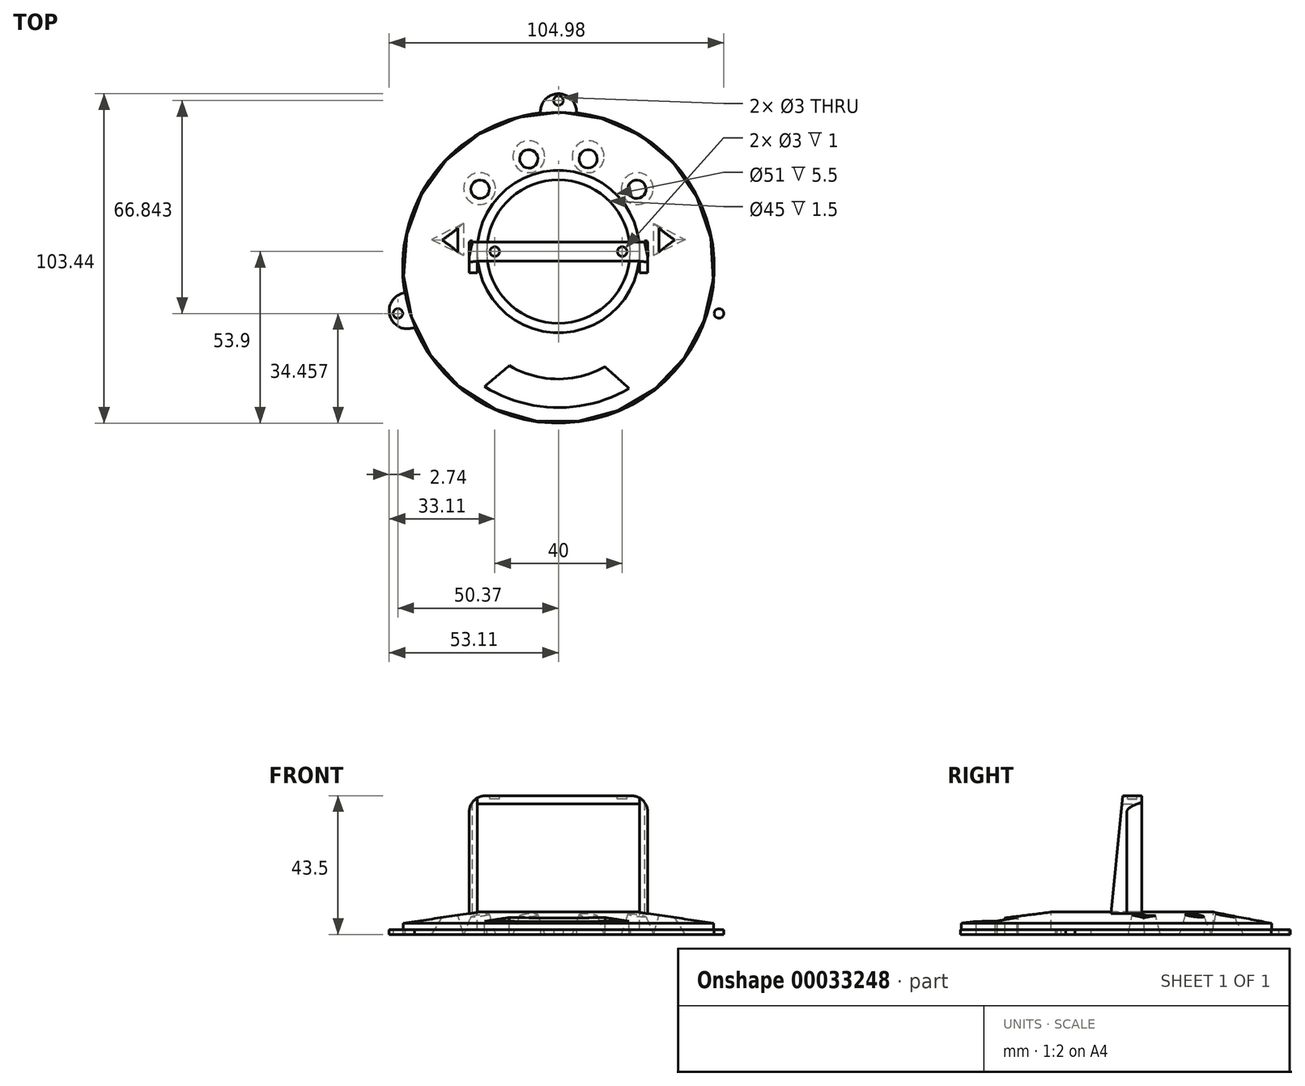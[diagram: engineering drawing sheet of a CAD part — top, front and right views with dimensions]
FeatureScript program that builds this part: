
annotation { "Feature Type Name" : "Feature", "Feature Type Description" : "" }
export const myFeature = defineFeature(function(context is Context, id is Id, definition is map)
    precondition{}
    {
        {
            var Q0;
            Q0=qCreatedBy(makeId("Top.planeOp"),FACE);
            var sketch = newSketch(context, id + "F0", { "sketchPlane" : qUnion([Q0])});
            skCircle(sketch, "E0", {"center": v(0, 0) * mm, "radius": 48.9 * mm});
            skArc(sketch, "E1", {"start": v(5.63, 48.57) * mm, "mid": v(0, 54.54) * mm, "end": v(-5.63, 48.57) * mm});
            skLineSegment(sketch, "E2", {"start": v(0, 48.9) * mm, "end": v(0, 52.4) * mm, "construction": true});
            skCircle(sketch, "E3", {"center": v(0, 52.4) * mm, "radius": 1.5 * mm});
            skCircle(sketch, "E4", {"center": v(-50.37, -14.44) * mm, "radius": 1.5 * mm});
            skArc(sketch, "E5", {"start": v(-48.24, -8.02) * mm, "mid": v(-52.9, -15.17) * mm, "end": v(-45.16, -18.76) * mm});
            skCircle(sketch, "E6.MirrorC", {"center": v(50.37, -14.44) * mm, "radius": 1.5 * mm});
            skArc(sketch, "E7.MirrorCS", {"start": v(48.24, -8.02) * mm, "mid": v(52.9, -15.17) * mm, "end": v(45.16, -18.76) * mm});
            skLineSegment(sketch, "E8", {"start": v(0, 0) * mm, "end": v(50.37, -14.44) * mm, "construction": true});
            skLineSegment(sketch, "E9", {"start": v(0, 0) * mm, "end": v(48.9, 0) * mm, "construction": true});
            skLineSegment(sketch, "E10.MirrorCS", {"start": v(0, 0) * mm, "end": v(-50.37, -14.44) * mm, "construction": true});
            skLineSegment(sketch, "E11.MirrorCS", {"start": v(0, 0) * mm, "end": v(-48.9, 0) * mm, "construction": true});
            skSolve(sketch);
        }
        {
            var Q0;
            {var subQ0=sQuery(id+"F0.wireOp",EDGE,"E0");var subQ12=makeQuery(id+"F0.imprint","IMPRINT",VERTEX,{"disambiguationData":[OD(0.0)],"derivedFrom":subQ0});Q0=makeQuery(id+"F0.imprint","IMPRINT",FACE,{"disambiguationData":[TD([[makeQuery(id+"F0.imprint","IMPRINT",EDGE,{"disambiguationData":[TD([[subQ12,1.0]])],"derivedFrom":subQ0}),1.0]])]});}
            var Q1;
            {var subQ0=sQuery(id+"F0.wireOp",EDGE,"E1");Q1=makeQuery(id+"F0.imprint","IMPRINT",FACE,{"disambiguationData":[TD([[makeQuery(id+"F0.imprint","IMPRINT",EDGE,{"derivedFrom":subQ0}),1.0]])]});}
            var Q2;
            {var subQ0=sQuery(id+"F0.wireOp",EDGE,"752fcca0-ccf0-49d4-acc3-ab4a65df21e3.2.0");Q2=makeQuery(id+"F0.imprint","IMPRINT",FACE,{"disambiguationData":[TD([[makeQuery(id+"F0.imprint","IMPRINT",EDGE,{"derivedFrom":subQ0}),1.0]])]});}
            var Q3;
            {var subQ0=sQuery(id+"F0.wireOp",EDGE,"752fcca0-ccf0-49d4-acc3-ab4a65df21e3.1.0");Q3=makeQuery(id+"F0.imprint","IMPRINT",FACE,{"disambiguationData":[TD([[makeQuery(id+"F0.imprint","IMPRINT",EDGE,{"derivedFrom":subQ0}),1.0]])]});}
            var Q4;
            Q4=makeQuery(id+"F0.imprint","IMPRINT",FACE,{"disambiguationData":[TD([[makeQuery(id+"F0.imprint","IMPRINT",EDGE,{"derivedFrom":sQuery(id+"F0.wireOp",EDGE,"E4")}),-1.0]])]});
            var Q5;
            Q5=makeQuery(id+"F0.imprint","IMPRINT",FACE,{"disambiguationData":[TD([[makeQuery(id+"F0.imprint","IMPRINT",EDGE,{"derivedFrom":sQuery(id+"F0.wireOp",EDGE,"E6.MirrorC")}),1.0]])]});
            var Q6;
            {var subQ0=sQuery(id+"F0.wireOp",EDGE,"E0");var subQ3=sQuery(id+"F0.wireOp",EDGE,"E1");var subQ4=makeQuery(id+"F0.imprint","INTERSECT",VERTEX,{"disambiguationData":[OD(0.0)],"derivedFrom":[subQ0,subQ3]});Q6=makeQuery(id+"F0.imprint","IMPRINT",FACE,{"disambiguationData":[TD([[makeQuery(id+"F0.imprint","IMPRINT",EDGE,{"disambiguationData":[TD([[subQ4,-1.0]])],"derivedFrom":subQ0}),1.0]])]});}
            extrude(context, id + "F1", {"entities" : qUnion([Q0, Q1, Q2, Q3, Q4, Q5, Q6]), "depth" : 1.5 * mm});
        }
        {
            var Q0;
            Q0=makeQuery(id+"F1.opExtrude","CAP_FACE",FACE,{"disambiguationData":[OSD([sQuery(id+"F0.wireOp",EDGE,"E0"),sQuery(id+"F0.wireOp",EDGE,"E1"),sQuery(id+"F0.wireOp",EDGE,"E3"),sQuery(id+"F0.wireOp",EDGE,"E4"),sQuery(id+"F0.wireOp",EDGE,"E5"),sQuery(id+"F0.wireOp",EDGE,"E6.MirrorC"),sQuery(id+"F0.wireOp",EDGE,"E7.MirrorCS")])],"isStart":false});
            var sketch = newSketch(context, id + "F2", { "sketchPlane" : qUnion([Q0])});
            skCircle(sketch, "E12", {"center": v(0, 0) * mm, "radius": 48.7 * mm});
            skSolve(sketch);
        }
        {
            var Q0;
            Q0=qSketchRegion(id+"F2",true);
            extrude(context, id + "F3", {"entities" : qUnion([Q0]), "operationType" : NewBodyOperationType.ADD, "depth" : 2 * mm});
        }
        {
            var Q0;
            Q0=qCreatedBy(makeId("Top.planeOp"),FACE);
            cPlane(context, id + "F4", {"entities" : qUnion([Q0]), "cplaneType" : CPlaneType.OFFSET, "offset" : 7 * mm, "width" : 150 * mm, "height" : 150 * mm});
        }
        {
            var Q0;
            Q0=qCreatedBy(id+"F4.planeOp",FACE);
            var sketch = newSketch(context, id + "F5", { "sketchPlane" : qUnion([Q0])});
            skCircle(sketch, "E13", {"center": v(0, 5) * mm, "radius": 25.5 * mm});
            skCircle(sketch, "E14.0", {"center": v(0, 52.4) * mm, "radius": 1.5 * mm});
            skLineSegment(sketch, "E15", {"start": v(0, 52.4) * mm, "end": v(0, 5) * mm, "construction": true});
            skSolve(sketch);
        }
        {
            var Q0;
            Q0=qCreatedBy(makeId("Top.planeOp"),FACE);
            var sketch = newSketch(context, id + "F6", { "sketchPlane" : qUnion([Q0])});
            skCircle(sketch, "E16", {"center": v(0, 0) * mm, "radius": 48.9 * mm});
            skSolve(sketch);
        }
        {
            var Q1;
            Q1=makeQuery(id+"F5.imprint","IMPRINT",FACE,{"disambiguationData":[TD([[makeQuery(id+"F5.imprint","IMPRINT",EDGE,{"derivedFrom":sQuery(id+"F5.wireOp",EDGE,"E13")}),1.0]])]});
            var Q2;
            Q2=makeQuery(id+"F3.opExtrude","CAP_FACE",FACE,{"disambiguationData":[OSD([sQuery(id+"F2.wireOp",EDGE,"E12")])],"isStart":false});
            loft(context, id + "F7", {"operationType" : NewBodyOperationType.ADD, "sheetProfilesArray" : [{ "sheetProfileEntities" : qUnion([Q1]) }, { "sheetProfileEntities" : qUnion([Q2]) }]});
        }
        {
            var Q0;
            Q0=makeQuery(id+"F1.opExtrude","CAP_FACE",FACE,{"disambiguationData":[OSD([sQuery(id+"F0.wireOp",EDGE,"E0"),sQuery(id+"F0.wireOp",EDGE,"E1"),sQuery(id+"F0.wireOp",EDGE,"E3"),sQuery(id+"F0.wireOp",EDGE,"752fcca0-ccf0-49d4-acc3-ab4a65df21e3.1.0"),sQuery(id+"F0.wireOp",EDGE,"752fcca0-ccf0-49d4-acc3-ab4a65df21e3.1.1"),sQuery(id+"F0.wireOp",EDGE,"752fcca0-ccf0-49d4-acc3-ab4a65df21e3.2.0"),sQuery(id+"F0.wireOp",EDGE,"752fcca0-ccf0-49d4-acc3-ab4a65df21e3.2.1")])],"isStart":false});
            var sketch = newSketch(context, id + "F8", { "sketchPlane" : qUnion([Q0])});
            skLineSegment(sketch, "E17", {"start": v(0, 0) * mm, "end": v(34, 0) * mm});
            skLineSegment(sketch, "E18", {"start": v(0, 0) * mm, "end": v(32.84, 8.8) * mm});
            skLineSegment(sketch, "E19", {"start": v(0, 0) * mm, "end": v(24.04, 24.04) * mm});
            skLineSegment(sketch, "E20", {"start": v(0, 0) * mm, "end": v(8.8, 32.84) * mm});
            skLineSegment(sketch, "E21", {"start": v(0, 0) * mm, "end": v(0, 34) * mm});
            skCircle(sketch, "E22", {"center": v(32.84, 8.8) * mm, "radius": 2.5 * mm});
            skCircle(sketch, "E23", {"center": v(24.04, 24.04) * mm, "radius": 2.5 * mm});
            skCircle(sketch, "E24", {"center": v(8.8, 32.84) * mm, "radius": 2.5 * mm});
            skCircle(sketch, "E25.MirrorC", {"center": v(-8.8, 32.84) * mm, "radius": 2.5 * mm});
            skCircle(sketch, "E26.MirrorC", {"center": v(-24.04, 24.04) * mm, "radius": 2.5 * mm});
            skCircle(sketch, "E27.MirrorC", {"center": v(-32.84, 8.8) * mm, "radius": 2.5 * mm});
            skSolve(sketch);
        }
        {
            var Q0;
            Q0=qCreatedBy(id+"F4.planeOp",FACE);
            var sketch = newSketch(context, id + "F9", { "sketchPlane" : qUnion([Q0])});
            skLineSegment(sketch, "E28", {"start": v(-24.4, 24.38) * mm, "end": v(0, 0) * mm, "construction": true});
            skLineSegment(sketch, "E29", {"start": v(0, 0) * mm, "end": v(-9.23, 33.76) * mm, "construction": true});
            skLineSegment(sketch, "E30", {"start": v(0, 0) * mm, "end": v(-31.88, 8.54) * mm, "construction": true});
            skLineSegment(sketch, "E31.MirrorCS", {"start": v(0, 0) * mm, "end": v(31.88, 8.54) * mm, "construction": true});
            skLineSegment(sketch, "E32.MirrorCS", {"start": v(24.4, 24.38) * mm, "end": v(0, 0) * mm, "construction": true});
            skLineSegment(sketch, "E33.MirrorCS", {"start": v(0, 0) * mm, "end": v(9.23, 33.76) * mm, "construction": true});
            skLineSegment(sketch, "E34", {"start": v(-31.88, 8.54) * mm, "end": v(-31.88, 12.04) * mm});
            skLineSegment(sketch, "E35", {"start": v(-31.88, 8.54) * mm, "end": v(-35.38, 8.54) * mm, "construction": true});
            skLineSegment(sketch, "E36", {"start": v(-31.88, 12.04) * mm, "end": v(-35.38, 8.54) * mm});
            skLineSegment(sketch, "E37.MirrorCS", {"start": v(-31.88, 5.04) * mm, "end": v(-35.38, 8.54) * mm});
            skLineSegment(sketch, "E38.MirrorCS", {"start": v(-31.88, 8.54) * mm, "end": v(-31.88, 5.04) * mm});
            skLineSegment(sketch, "E39.MirrorCS", {"start": v(31.88, 8.54) * mm, "end": v(31.88, 12.04) * mm});
            skLineSegment(sketch, "E40.MirrorCS", {"start": v(31.88, 12.04) * mm, "end": v(35.38, 8.54) * mm});
            skLineSegment(sketch, "E41.MirrorCS", {"start": v(31.88, 5.04) * mm, "end": v(35.38, 8.54) * mm});
            skLineSegment(sketch, "E42.MirrorCS", {"start": v(31.88, 8.54) * mm, "end": v(31.88, 5.04) * mm});
            skCircle(sketch, "E43", {"center": v(9.23, 33.76) * mm, "radius": 2.5 * mm});
            skCircle(sketch, "E44", {"center": v(-9.23, 33.76) * mm, "radius": 2.5 * mm});
            skCircle(sketch, "E45", {"center": v(-24.4, 24.38) * mm, "radius": 2.5 * mm});
            skCircle(sketch, "E46", {"center": v(24.4, 24.38) * mm, "radius": 2.5 * mm});
            skSolve(sketch);
        }
        {
            var Q0;
            Q0=makeQuery(id+"F1.opExtrude","CAP_FACE",FACE,{"disambiguationData":[OSD([sQuery(id+"F0.wireOp",EDGE,"E0"),sQuery(id+"F0.wireOp",EDGE,"E1"),sQuery(id+"F0.wireOp",EDGE,"E3"),sQuery(id+"F0.wireOp",EDGE,"752fcca0-ccf0-49d4-acc3-ab4a65df21e3.1.0"),sQuery(id+"F0.wireOp",EDGE,"752fcca0-ccf0-49d4-acc3-ab4a65df21e3.1.1"),sQuery(id+"F0.wireOp",EDGE,"752fcca0-ccf0-49d4-acc3-ab4a65df21e3.2.0"),sQuery(id+"F0.wireOp",EDGE,"752fcca0-ccf0-49d4-acc3-ab4a65df21e3.2.1")])],"isStart":false});
            var sketch = newSketch(context, id + "F10", { "sketchPlane" : qUnion([Q0])});
            skLineSegment(sketch, "E47", {"start": v(-15.4, -30.8) * mm, "end": v(-23.2, -37.4) * mm});
            skArc(sketch, "E48", {"start": v(-23.2, -37.4) * mm, "mid": v(-0.58, -44) * mm, "end": v(22.2, -37.99) * mm});
            skLineSegment(sketch, "E49", {"start": v(-15.4, -30.8) * mm, "end": v(14.6, -31.2) * mm, "construction": true});
            skLineSegment(sketch, "E50", {"start": v(0, 0) * mm, "end": v(-0.4, -31) * mm, "construction": true});
            skArc(sketch, "E51", {"start": v(-15.4, -30.8) * mm, "mid": v(-0.46, -35.02) * mm, "end": v(14.6, -31.2) * mm});
            skLineSegment(sketch, "E52.MirrorCS", {"start": v(14.6, -31.2) * mm, "end": v(22.2, -37.99) * mm});
            skSolve(sketch);
        }
        {
            var Q0;
            Q0=qSketchRegion(id+"F10",true);
            extrude(context, id + "F11", {"entities" : qUnion([Q0]), "operationType" : NewBodyOperationType.REMOVE, "endBound" : BoundingType.THROUGH_ALL, "oppositeDirection" : true, "depth" : 25 * mm, "hasSecondDirection" : true, "secondDirectionBound" : SecondDirectionBoundingType.THROUGH_ALL, "secondDirectionOppositeDirection" : false, "secondDirectionDepth" : 25 * mm});
        }
        {
            var Q0;
            Q0=makeQuery(id+"F1.opExtrude","CAP_FACE",FACE,{"disambiguationData":[OSD([sQuery(id+"F0.wireOp",EDGE,"E0"),sQuery(id+"F0.wireOp",EDGE,"E1"),sQuery(id+"F0.wireOp",EDGE,"E3"),sQuery(id+"F0.wireOp",EDGE,"752fcca0-ccf0-49d4-acc3-ab4a65df21e3.1.0"),sQuery(id+"F0.wireOp",EDGE,"752fcca0-ccf0-49d4-acc3-ab4a65df21e3.1.1"),sQuery(id+"F0.wireOp",EDGE,"752fcca0-ccf0-49d4-acc3-ab4a65df21e3.2.0"),sQuery(id+"F0.wireOp",EDGE,"752fcca0-ccf0-49d4-acc3-ab4a65df21e3.2.1")])],"isStart":true});
            var sketch = newSketch(context, id + "F12", { "sketchPlane" : qUnion([Q0])});
            skLineSegment(sketch, "E53.0", {"start": v(0, 0) * mm, "end": v(0, -34) * mm, "construction": true});
            skLineSegment(sketch, "E54", {"start": v(-32.84, -8.8) * mm, "end": v(-39.84, -8.8) * mm, "construction": true});
            skLineSegment(sketch, "E55", {"start": v(-29.84, -13.8) * mm, "end": v(-39.84, -8.8) * mm});
            skLineSegment(sketch, "E56", {"start": v(-32.84, -8.8) * mm, "end": v(-29.84, -8.8) * mm, "construction": true});
            skLineSegment(sketch, "E57", {"start": v(-29.84, -8.8) * mm, "end": v(-29.84, -13.8) * mm});
            skLineSegment(sketch, "E58", {"start": v(-29.84, -8.8) * mm, "end": v(-29.84, -3.8) * mm});
            skLineSegment(sketch, "E59", {"start": v(-39.84, -8.8) * mm, "end": v(-29.84, -3.8) * mm});
            skLineSegment(sketch, "E60.MirrorCS", {"start": v(29.84, -8.8) * mm, "end": v(29.84, -13.8) * mm});
            skLineSegment(sketch, "E61.MirrorCS", {"start": v(29.84, -13.8) * mm, "end": v(39.84, -8.8) * mm});
            skLineSegment(sketch, "E62.MirrorCS", {"start": v(39.84, -8.8) * mm, "end": v(29.84, -3.8) * mm});
            skLineSegment(sketch, "E63.MirrorCS", {"start": v(29.84, -8.8) * mm, "end": v(29.84, -3.8) * mm});
            skPoint(sketch, "E64.MirrorP", {"position": v(9.32, -34.77) * mm});
            skPoint(sketch, "E65.MirrorP", {"position": v(32.84, -8.8) * mm});
            skPoint(sketch, "E66.MirrorP", {"position": v(24.75, -24.75) * mm});
            skLineSegment(sketch, "E67", {"start": v(0, 0) * mm, "end": v(32.84, -8.8) * mm, "construction": true});
            skLineSegment(sketch, "E68", {"start": v(32.84, -8.8) * mm, "end": v(29.84, -8.8) * mm, "construction": true});
            skLineSegment(sketch, "E69", {"start": v(0, 0) * mm, "end": v(24.75, -24.75) * mm, "construction": true});
            skLineSegment(sketch, "E70", {"start": v(0, 0) * mm, "end": v(9.32, -34.77) * mm, "construction": true});
            skPoint(sketch, "E71.MirrorP", {"position": v(-24.75, -24.75) * mm});
            skPoint(sketch, "E72.MirrorP", {"position": v(-9.32, -34.77) * mm});
            skCircle(sketch, "E73", {"center": v(24.75, -24.75) * mm, "radius": 5 * mm});
            skCircle(sketch, "E74", {"center": v(9.32, -34.77) * mm, "radius": 5 * mm});
            skCircle(sketch, "E75", {"center": v(-9.32, -34.77) * mm, "radius": 5 * mm});
            skCircle(sketch, "E76", {"center": v(-24.75, -24.75) * mm, "radius": 5 * mm});
            skSolve(sketch);
        }
        {
            var Q1;
            Q1=makeQuery(id+"F12.imprint","IMPRINT",FACE,{"disambiguationData":[TD([[makeQuery(id+"F12.imprint","IMPRINT",EDGE,{"derivedFrom":sQuery(id+"F12.wireOp",EDGE,"E60.MirrorCS")}),1.0]])]});
            var Q2;
            Q2=makeQuery(id+"F9.imprint","IMPRINT",FACE,{"disambiguationData":[TD([[makeQuery(id+"F9.imprint","IMPRINT",EDGE,{"derivedFrom":sQuery(id+"F9.wireOp",EDGE,"E39.MirrorCS")}),-1.0]])]});
            loft(context, id + "F13", {"operationType" : NewBodyOperationType.REMOVE, "sheetProfilesArray" : [{ "sheetProfileEntities" : qUnion([Q1]) }, { "sheetProfileEntities" : qUnion([Q2]) }]});
        }
        {
            var Q1;
            Q1=makeQuery(id+"F12.imprint","IMPRINT",FACE,{"disambiguationData":[TD([[makeQuery(id+"F12.imprint","IMPRINT",EDGE,{"derivedFrom":sQuery(id+"F12.wireOp",EDGE,"E73")}),1.0]])]});
            var Q2;
            Q2=makeQuery(id+"F9.imprint","IMPRINT",FACE,{"disambiguationData":[TD([[makeQuery(id+"F9.imprint","IMPRINT",EDGE,{"derivedFrom":sQuery(id+"F9.wireOp",EDGE,"E46")}),1.0]])]});
            loft(context, id + "F14", {"operationType" : NewBodyOperationType.REMOVE, "sheetProfilesArray" : [{ "sheetProfileEntities" : qUnion([Q1]) }, { "sheetProfileEntities" : qUnion([Q2]) }]});
        }
        {
            var Q1;
            Q1=makeQuery(id+"F12.imprint","IMPRINT",FACE,{"disambiguationData":[TD([[makeQuery(id+"F12.imprint","IMPRINT",EDGE,{"derivedFrom":sQuery(id+"F12.wireOp",EDGE,"E74")}),1.0]])]});
            var Q2;
            Q2=makeQuery(id+"F9.imprint","IMPRINT",FACE,{"disambiguationData":[TD([[makeQuery(id+"F9.imprint","IMPRINT",EDGE,{"derivedFrom":sQuery(id+"F9.wireOp",EDGE,"E43")}),1.0]])]});
            loft(context, id + "F15", {"operationType" : NewBodyOperationType.REMOVE, "sheetProfilesArray" : [{ "sheetProfileEntities" : qUnion([Q1]) }, { "sheetProfileEntities" : qUnion([Q2]) }]});
        }
        {
            var Q1;
            Q1=makeQuery(id+"F12.imprint","IMPRINT",FACE,{"disambiguationData":[TD([[makeQuery(id+"F12.imprint","IMPRINT",EDGE,{"derivedFrom":sQuery(id+"F12.wireOp",EDGE,"E75")}),1.0]])]});
            var Q2;
            Q2=makeQuery(id+"F9.imprint","IMPRINT",FACE,{"disambiguationData":[TD([[makeQuery(id+"F9.imprint","IMPRINT",EDGE,{"derivedFrom":sQuery(id+"F9.wireOp",EDGE,"E44")}),1.0]])]});
            loft(context, id + "F16", {"operationType" : NewBodyOperationType.REMOVE, "sheetProfilesArray" : [{ "sheetProfileEntities" : qUnion([Q1]) }, { "sheetProfileEntities" : qUnion([Q2]) }]});
        }
        {
            var Q1;
            Q1=makeQuery(id+"F12.imprint","IMPRINT",FACE,{"disambiguationData":[TD([[makeQuery(id+"F12.imprint","IMPRINT",EDGE,{"derivedFrom":sQuery(id+"F12.wireOp",EDGE,"E76")}),1.0]])]});
            var Q2;
            Q2=makeQuery(id+"F9.imprint","IMPRINT",FACE,{"disambiguationData":[TD([[makeQuery(id+"F9.imprint","IMPRINT",EDGE,{"derivedFrom":sQuery(id+"F9.wireOp",EDGE,"E45")}),1.0]])]});
            loft(context, id + "F17", {"operationType" : NewBodyOperationType.REMOVE, "sheetProfilesArray" : [{ "sheetProfileEntities" : qUnion([Q1]) }, { "sheetProfileEntities" : qUnion([Q2]) }]});
        }
        {
            var Q1;
            Q1=makeQuery(id+"F12.imprint","IMPRINT",FACE,{"disambiguationData":[TD([[makeQuery(id+"F12.imprint","IMPRINT",EDGE,{"derivedFrom":sQuery(id+"F12.wireOp",EDGE,"E55")}),-1.0]])]});
            var Q2;
            Q2=makeQuery(id+"F9.imprint","IMPRINT",FACE,{"disambiguationData":[TD([[makeQuery(id+"F9.imprint","IMPRINT",EDGE,{"derivedFrom":sQuery(id+"F9.wireOp",EDGE,"E34")}),1.0]])]});
            loft(context, id + "F18", {"operationType" : NewBodyOperationType.REMOVE, "sheetProfilesArray" : [{ "sheetProfileEntities" : qUnion([Q1]) }, { "sheetProfileEntities" : qUnion([Q2]) }]});
        }
        {
            var Q0;
            Q0=qSketchRegion(id+"F5",true);
            extrude(context, id + "F19", {"entities" : qUnion([Q0]), "operationType" : NewBodyOperationType.REMOVE, "oppositeDirection" : true, "depth" : 5.5 * mm});
        }
        {
            var Q0;
            Q0=makeQuery(id+"F6.imprint","IMPRINT",FACE,{"disambiguationData":[TD([[makeQuery(id+"F6.imprint","IMPRINT",EDGE,{"derivedFrom":sQuery(id+"F6.wireOp",EDGE,"E16")}),1.0]])]});
            var sketch = newSketch(context, id + "F20", { "sketchPlane" : qUnion([Q0])});
            skPoint(sketch, "E77.rect.middle", {"position": v(0, 0) * mm});
            skCircle(sketch, "E78.0", {"center": v(0, 52.4) * mm, "radius": 1.5 * mm, "construction": true});
            skCircle(sketch, "E79.0", {"center": v(0, 5) * mm, "radius": 25.5 * mm, "construction": true});
            skCircle(sketch, "E80", {"center": v(0, 5) * mm, "radius": 22.5 * mm});
            skSolve(sketch);
        }
        {
            var Q0;
            Q0=qSketchRegion(id+"F20",true);
            extrude(context, id + "F21", {"entities" : qUnion([Q0]), "operationType" : NewBodyOperationType.REMOVE, "endBound" : BoundingType.THROUGH_ALL, "depth" : 25 * mm});
        }
        {
            var Q0;
            Q0=qCreatedBy(makeId("Front.planeOp"),FACE);
            var Q1;
            Q1=sQuery(id+"F5.wireOp",VERTEX,"E13.center");
            cPlane(context, id + "F22", {"entities" : qUnion([Q0, Q1]), "cplaneType" : CPlaneType.PLANE_POINT, "offset" : 0 * mm, "oppositeDirection" : true, "width" : 150 * mm, "height" : 150 * mm});
        }
        {
            var Q0;
            Q0=qCreatedBy(id+"F22.planeOp",FACE);
            var sketch = newSketch(context, id + "F23", { "sketchPlane" : qUnion([Q0])});
            skPoint(sketch, "E81.0", {"position": v(0, 7) * mm});
            skLineSegment(sketch, "E82.0", {"start": v(-25.5, 7) * mm, "end": v(25.5, 7) * mm, "construction": true});
            skLineSegment(sketch, "E83.0", {"start": v(-25.5, 1.5) * mm, "end": v(25.5, 1.5) * mm, "construction": true});
            skLineSegment(sketch, "E84", {"start": v(25.5, 1.5) * mm, "end": v(25.5, 41.5) * mm});
            skLineSegment(sketch, "E85", {"start": v(25.5, 41.5) * mm, "end": v(0, 41.5) * mm});
            skLineSegment(sketch, "E86", {"start": v(0, 41.5) * mm, "end": v(0, 43.5) * mm, "construction": true});
            skLineSegment(sketch, "E87", {"start": v(0, 43.5) * mm, "end": v(28, 43.5) * mm});
            skLineSegment(sketch, "E88.MirrorCS", {"start": v(-25.5, 41.5) * mm, "end": v(0, 41.5) * mm});
            skLineSegment(sketch, "E89.MirrorCS", {"start": v(-25.5, 1.5) * mm, "end": v(-25.5, 41.5) * mm});
            skLineSegment(sketch, "E90.MirrorCS", {"start": v(0, 43.5) * mm, "end": v(-28, 43.5) * mm});
            skLineSegment(sketch, "E91", {"start": v(25.5, 1.5) * mm, "end": v(28, 1.5) * mm});
            skLineSegment(sketch, "E92", {"start": v(28, 1.5) * mm, "end": v(28, 43.5) * mm});
            skLineSegment(sketch, "E93.MirrorCS", {"start": v(-25.5, 1.5) * mm, "end": v(-28, 1.5) * mm});
            skLineSegment(sketch, "E94.MirrorCS", {"start": v(-28, 1.5) * mm, "end": v(-28, 43.5) * mm});
            skSolve(sketch);
        }
        {
            var Q0;
            Q0 = qSketchRegion(id + "F23", true);
            extrude(context, id + "F24", {"entities" : qUnion([Q0]), "operationType" : NewBodyOperationType.ADD, "depth" : 3 * mm, "hasSecondDirection" : true, "secondDirectionOppositeDirection" : true, "secondDirectionDepth" : 3 * mm});
        }
        {
            var Q0;
            Q0=makeQuery(id+"F24.opExtrude","SWEPT_FACE",FACE,{"disambiguationData":[OSD([sQuery(id+"F23.wireOp",EDGE,"E87"),sQuery(id+"F23.wireOp",EDGE,"E90.MirrorCS")])]});
            var sketch = newSketch(context, id + "F25", { "sketchPlane" : qUnion([Q0])});
            skPoint(sketch, "E95.0", {"position": v(0, 5) * mm});
            skLineSegment(sketch, "E96", {"start": v(20, 5) * mm, "end": v(-20, 5) * mm, "construction": true});
            skCircle(sketch, "E97", {"center": v(20, 5) * mm, "radius": 1.5 * mm});
            skCircle(sketch, "E98.MirrorC", {"center": v(-20, 5) * mm, "radius": 1.5 * mm});
            skSolve(sketch);
        }
        {
            var Q0;
            Q0 = qSketchRegion(id + "F25", true);
            extrude(context, id + "F26", {"entities" : qUnion([Q0]), "operationType" : NewBodyOperationType.REMOVE, "oppositeDirection" : true, "depth" : 1 * mm});
        }
        {
            var Q0;
            Q0=makeQuery(id+"F24.opExtrude","SWEPT_FACE",FACE,{"disambiguationData":[OSD([sQuery(id+"F23.wireOp",EDGE,"E94.MirrorCS")])]});
            var sketch = newSketch(context, id + "F27", { "sketchPlane" : qUnion([Q0])});
            skLineSegment(sketch, "E99", {"start": v(-2, 43.5) * mm, "end": v(-2, 3.5) * mm});
            skLineSegment(sketch, "E100", {"start": v(-2, 3.5) * mm, "end": v(2, 3.5) * mm});
            skLineSegment(sketch, "E101", {"start": v(2, 3.5) * mm, "end": v(-2, 43.5) * mm});
            skSolve(sketch);
        }
        {
            var Q0;
            Q0 = qSketchRegion(id + "F27", true);
            extrude(context, id + "F28", {"entities" : qUnion([Q0]), "operationType" : NewBodyOperationType.ADD, "oppositeDirection" : true, "depth" : 2.5 * mm});
        }
        {
            var Q0;
            Q0=makeQuery(id+"F24.opExtrude","SWEPT_FACE",FACE,{"disambiguationData":[OSD([sQuery(id+"F23.wireOp",EDGE,"E92")])]});
            var sketch = newSketch(context, id + "F29", { "sketchPlane" : qUnion([Q0])});
            skLineSegment(sketch, "E102", {"start": v(2, 43.5) * mm, "end": v(2, 3.5) * mm});
            skLineSegment(sketch, "E103", {"start": v(2, 3.5) * mm, "end": v(-2, 3.5) * mm});
            skLineSegment(sketch, "E104", {"start": v(-2, 3.5) * mm, "end": v(2, 43.5) * mm});
            skSolve(sketch);
        }
        {
            var Q0;
            Q0 = qSketchRegion(id + "F29", true);
            extrude(context, id + "F30", {"entities" : qUnion([Q0]), "operationType" : NewBodyOperationType.ADD, "oppositeDirection" : true, "depth" : 2.5 * mm});
        }
        {
            var Q0;
            Q0=makeQuery(id+"F24.opExtrude","SWEPT_FACE",FACE,{"disambiguationData":[OSD([sQuery(id+"F23.wireOp",EDGE,"E85"),sQuery(id+"F23.wireOp",EDGE,"E88.MirrorCS")])]});
            var sketch = newSketch(context, id + "F31", { "sketchPlane" : qUnion([Q0])});
            skLineSegment(sketch, "E105.bottom", {"start": v(25.5, -2) * mm, "end": v(-25.5, -2) * mm});
            skLineSegment(sketch, "E105.top", {"start": v(25.5, -8) * mm, "end": v(-25.5, -8) * mm});
            skLineSegment(sketch, "E105.left", {"start": v(25.5, -2) * mm, "end": v(25.5, -8) * mm});
            skLineSegment(sketch, "E105.right", {"start": v(-25.5, -2) * mm, "end": v(-25.5, -8) * mm});
            skSolve(sketch);
        }
        {
            var Q0;
            Q0 = qSketchRegion(id + "F31", true);
            extrude(context, id + "F32", {"entities" : qUnion([Q0]), "operationType" : NewBodyOperationType.ADD, "depth" : .5 * mm});
        }
        {
            var Q0;
            Q0=makeQuery(id+"F24.opExtrude","SWEPT_EDGE",EDGE,{"disambiguationData":[OSD([sQuery(id+"F23.wireOp",EDGE,"E90.MirrorCS"),sQuery(id+"F23.wireOp",EDGE,"E94.MirrorCS")])]});
            var Q1;
            Q1=makeQuery(id+"F24.opExtrude","SWEPT_EDGE",EDGE,{"disambiguationData":[OSD([sQuery(id+"F23.wireOp",EDGE,"E87"),sQuery(id+"F23.wireOp",EDGE,"E92")])]});
            fillet(context, id + "F33", {"entities" : qUnion([Q0, Q1]), "radius" : 5 * mm, "tangentPropagation" : true, "allowEdgeOverflow" : false});
        }
        {
            var Q0;
            Q0=makeQuery(id+"F24.opExtrude","SWEPT_FACE",FACE,{"disambiguationData":[OSD([sQuery(id+"F23.wireOp",EDGE,"E87"),sQuery(id+"F23.wireOp",EDGE,"E90.MirrorCS")])]});
            var sketch = newSketch(context, id + "F34", { "sketchPlane" : qUnion([Q0])});
            skLineSegment(sketch, "E106", {"start": v(-28.97, -1.44) * mm, "end": v(-26.97, 8.36) * mm});
            skLineSegment(sketch, "E107", {"start": v(-26.97, 8.36) * mm, "end": v(-28.97, 8.36) * mm});
            skLineSegment(sketch, "E108", {"start": v(-28.97, 8.36) * mm, "end": v(-28.97, -1.44) * mm});
            skLineSegment(sketch, "E109.MirrorCS", {"start": v(28.97, -1.44) * mm, "end": v(26.97, 8.36) * mm});
            skLineSegment(sketch, "E110.MirrorCS", {"start": v(26.97, 8.36) * mm, "end": v(28.97, 8.36) * mm});
            skLineSegment(sketch, "E111.MirrorCS", {"start": v(28.97, 8.36) * mm, "end": v(28.97, -1.44) * mm});
            skSolve(sketch);
        }
        {
            var Q0;
            Q0 = qSketchRegion(id + "F34", true);
            extrude(context, id + "F35", {"entities" : qUnion([Q0]), "operationType" : NewBodyOperationType.REMOVE, "oppositeDirection" : true, "depth" : 36.9 * mm});
        }
    });
